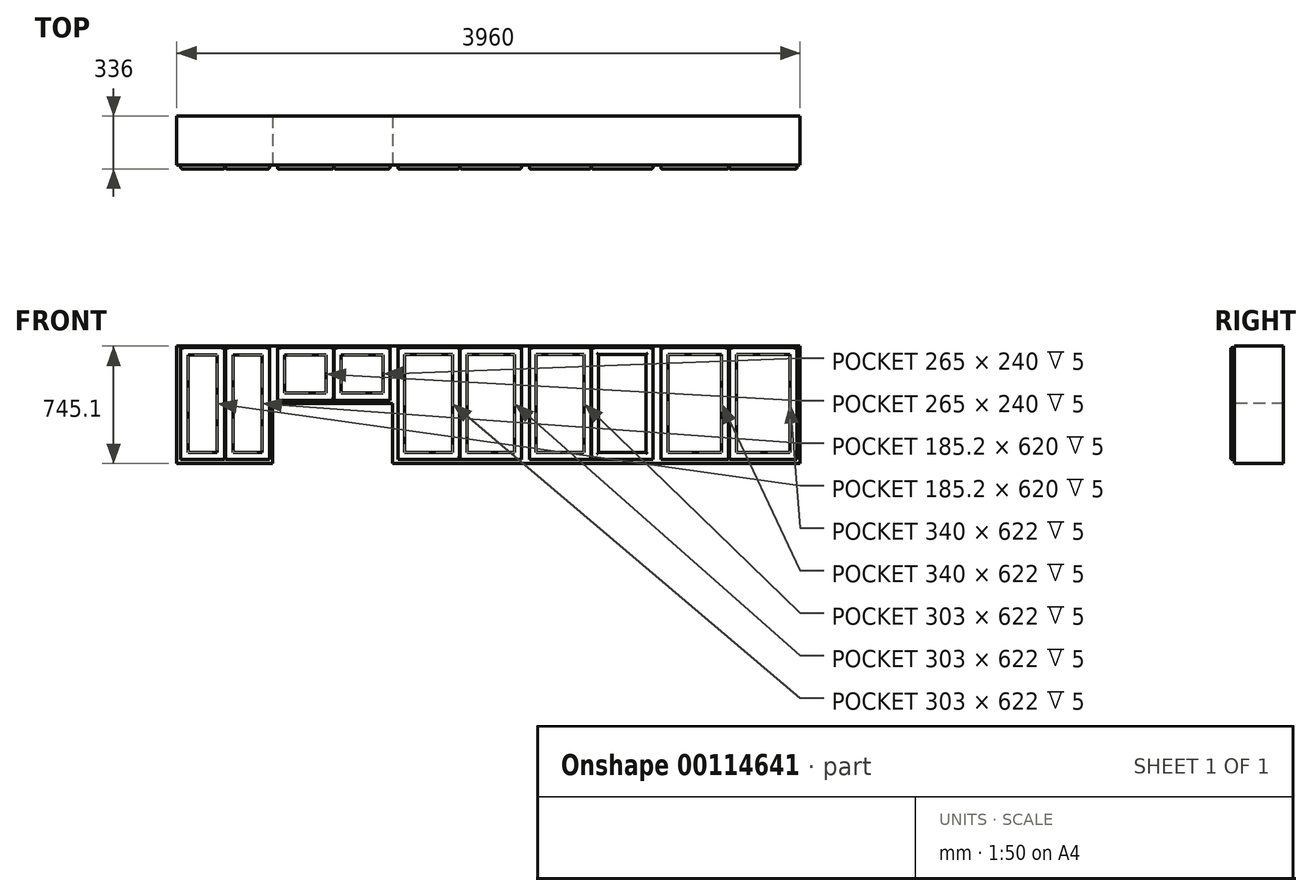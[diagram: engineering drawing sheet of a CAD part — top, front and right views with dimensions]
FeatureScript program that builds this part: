
annotation { "Feature Type Name" : "Feature", "Feature Type Description" : "" }
export const myFeature = defineFeature(function(context is Context, id is Id, definition is map)
    precondition{}
    {
        {
            var Q0;
            Q0=qCreatedBy(makeId("Front.planeOp"),FACE);
            var sketch = newSketch(context, id + "F0", { "sketchPlane" : qUnion([Q0])});
            skLineSegment(sketch, "E0.bottom", {"start": v(1980, -372.55) * mm, "end": v(-1980, -372.55) * mm});
            skLineSegment(sketch, "E0.top", {"start": v(1980, 372.55) * mm, "end": v(-1980, 372.55) * mm});
            skLineSegment(sketch, "E0.left", {"start": v(1980, -372.55) * mm, "end": v(1980, 372.55) * mm});
            skLineSegment(sketch, "E0.right", {"start": v(-1980, -372.55) * mm, "end": v(-1980, 372.55) * mm});
            skPoint(sketch, "E0.middle", {"position": v(0, 0) * mm});
            skSolve(sketch);
        }
        {
            var Q0;
            Q0=makeQuery(id+"F0.imprint","IMPRINT",FACE,{"disambiguationData":[TD([[makeQuery(id+"F0.imprint","IMPRINT",EDGE,{"derivedFrom":sQuery(id+"F0.wireOp",EDGE,"E0.bottom")}),-1.0]])]});
            extrude(context, id + "F1", {"entities" : qUnion([Q0]), "depth" : 311 * mm});
        }
        {
            var Q0;
            Q0=makeQuery(id+"F1.opExtrude","CAP_FACE",FACE,{"disambiguationData":[OSD([sQuery(id+"F0.wireOp",EDGE,"E0.bottom"),sQuery(id+"F0.wireOp",EDGE,"E0.top"),sQuery(id+"F0.wireOp",EDGE,"E0.left"),sQuery(id+"F0.wireOp",EDGE,"E0.right")])],"isStart":false});
            var sketch = newSketch(context, id + "F2", { "sketchPlane" : qUnion([Q0])});
            skLineSegment(sketch, "E1", {"start": v(-1370, -372.55) * mm, "end": v(-1370, 7.45) * mm});
            skLineSegment(sketch, "E2", {"start": v(-1370, 7.45) * mm, "end": v(-610, 7.45) * mm});
            skLineSegment(sketch, "E3", {"start": v(-610, 7.45) * mm, "end": v(-610, -372.55) * mm});
            skSolve(sketch);
        }
        {
            var Q0;
            {var subQ0=sQuery(id+"F2.wireOp",EDGE,"E1");Q0=makeQuery(id+"F2.imprint","IMPRINT",FACE,{"disambiguationData":[TD([[makeQuery(id+"F2.imprint","IMPRINT",EDGE,{"derivedFrom":subQ0}),-1.0]])]});}
            extrude(context, id + "F3", {"entities" : qUnion([Q0]), "operationType" : NewBodyOperationType.REMOVE, "endBound" : BoundingType.THROUGH_ALL, "oppositeDirection" : true, "depth" : 25 * mm});
        }
        {
            var Q0;
            Q0=makeQuery(id+"F1.opExtrude","CAP_FACE",FACE,{"disambiguationData":[OSD([sQuery(id+"F0.wireOp",EDGE,"E0.bottom"),sQuery(id+"F0.wireOp",EDGE,"E0.top"),sQuery(id+"F0.wireOp",EDGE,"E0.left"),sQuery(id+"F0.wireOp",EDGE,"E0.right")])],"isStart":false});
            var sketch = newSketch(context, id + "F4", { "sketchPlane" : qUnion([Q0])});
            skPoint(sketch, "E4.oppositeSnap0", {"position": v(-1675, -372.55) * mm});
            skLineSegment(sketch, "E4.bottom", {"start": v(-1955, 362.45) * mm, "end": v(-1675, 362.45) * mm});
            skLineSegment(sketch, "E4.top", {"start": v(-1955, -347.55) * mm, "end": v(-1675, -347.55) * mm});
            skLineSegment(sketch, "E4.left", {"start": v(-1955, 362.45) * mm, "end": v(-1955, -347.55) * mm});
            skLineSegment(sketch, "E4.right", {"start": v(-1675, 362.45) * mm, "end": v(-1675, -347.55) * mm});
            skLineSegment(sketch, "E5.bottom", {"start": v(-1670, 362.45) * mm, "end": v(-1390, 362.45) * mm});
            skLineSegment(sketch, "E5.top", {"start": v(-1670, -347.55) * mm, "end": v(-1390, -347.55) * mm});
            skLineSegment(sketch, "E5.left", {"start": v(-1670, 362.45) * mm, "end": v(-1670, -347.55) * mm});
            skLineSegment(sketch, "E5.right", {"start": v(-1390, 362.45) * mm, "end": v(-1390, -347.55) * mm});
            skLineSegment(sketch, "E6.bottom", {"start": v(-1340, 362.45) * mm, "end": v(-985, 362.45) * mm});
            skLineSegment(sketch, "E6.top", {"start": v(-1340, 27.45) * mm, "end": v(-985, 27.45) * mm});
            skLineSegment(sketch, "E6.left", {"start": v(-1340, 362.45) * mm, "end": v(-1340, 27.45) * mm});
            skLineSegment(sketch, "E6.right", {"start": v(-985, 362.45) * mm, "end": v(-985, 27.45) * mm});
            skLineSegment(sketch, "E7.bottom", {"start": v(-980, 362.45) * mm, "end": v(-625, 362.45) * mm});
            skLineSegment(sketch, "E7.top", {"start": v(-980, 27.45) * mm, "end": v(-625, 27.45) * mm});
            skLineSegment(sketch, "E7.left", {"start": v(-980, 362.45) * mm, "end": v(-980, 27.45) * mm});
            skLineSegment(sketch, "E7.right", {"start": v(-625, 362.45) * mm, "end": v(-625, 27.45) * mm});
            skLineSegment(sketch, "E8.bottom", {"start": v(-575, 362.45) * mm, "end": v(-185, 362.45) * mm});
            skLineSegment(sketch, "E8.top", {"start": v(-575, -347.55) * mm, "end": v(-185, -347.55) * mm});
            skLineSegment(sketch, "E8.left", {"start": v(-575, 362.45) * mm, "end": v(-575, -347.55) * mm});
            skLineSegment(sketch, "E8.right", {"start": v(-185, 362.45) * mm, "end": v(-185, -347.55) * mm});
            skLineSegment(sketch, "E9.bottom", {"start": v(-180, 362.45) * mm, "end": v(210, 362.45) * mm});
            skLineSegment(sketch, "E9.top", {"start": v(-180, -347.55) * mm, "end": v(210, -347.55) * mm});
            skLineSegment(sketch, "E9.left", {"start": v(-180, 362.45) * mm, "end": v(-180, -347.55) * mm});
            skLineSegment(sketch, "E9.right", {"start": v(210, 362.45) * mm, "end": v(210, -347.55) * mm});
            skLineSegment(sketch, "E10.bottom", {"start": v(260, 362.45) * mm, "end": v(650, 362.45) * mm});
            skLineSegment(sketch, "E10.top", {"start": v(260, -347.55) * mm, "end": v(650, -347.55) * mm});
            skLineSegment(sketch, "E10.left", {"start": v(260, 362.45) * mm, "end": v(260, -347.55) * mm});
            skLineSegment(sketch, "E10.right", {"start": v(650, 362.45) * mm, "end": v(650, -347.55) * mm});
            skLineSegment(sketch, "E11.bottom", {"start": v(655, 362.45) * mm, "end": v(1045, 362.45) * mm});
            skLineSegment(sketch, "E11.top", {"start": v(655, -347.55) * mm, "end": v(1045, -347.55) * mm});
            skLineSegment(sketch, "E11.left", {"start": v(655, 362.45) * mm, "end": v(655, -347.55) * mm});
            skLineSegment(sketch, "E11.right", {"start": v(1045, 362.45) * mm, "end": v(1045, -347.55) * mm});
            skLineSegment(sketch, "E12.bottom", {"start": v(1095, 362.45) * mm, "end": v(1525, 362.45) * mm});
            skLineSegment(sketch, "E12.top", {"start": v(1095, -347.55) * mm, "end": v(1525, -347.55) * mm});
            skLineSegment(sketch, "E12.left", {"start": v(1095, 362.45) * mm, "end": v(1095, -347.55) * mm});
            skLineSegment(sketch, "E12.right", {"start": v(1525, 362.45) * mm, "end": v(1525, -347.55) * mm});
            skLineSegment(sketch, "E13.bottom", {"start": v(1530, 362.45) * mm, "end": v(1960, 362.45) * mm});
            skLineSegment(sketch, "E13.top", {"start": v(1530, -347.55) * mm, "end": v(1960, -347.55) * mm});
            skLineSegment(sketch, "E13.left", {"start": v(1530, 362.45) * mm, "end": v(1530, -347.55) * mm});
            skLineSegment(sketch, "E13.right", {"start": v(1960, 362.45) * mm, "end": v(1960, -347.55) * mm});
            skSolve(sketch);
        }
        {
            var Q0;
            Q0 = qSketchRegion(id + "F4", true);
            extrude(context, id + "F5", {"entities" : qUnion([Q0]), "operationType" : NewBodyOperationType.ADD, "depth" : 25 * mm});
        }
        {
            var Q0;
            Q0=makeQuery(id+"F5.opExtrude","CAP_FACE",FACE,{"disambiguationData":[OSD([sQuery(id+"F4.wireOp",EDGE,"E4.bottom"),sQuery(id+"F4.wireOp",EDGE,"E4.top"),sQuery(id+"F4.wireOp",EDGE,"E4.left"),sQuery(id+"F4.wireOp",EDGE,"E4.right")])],"isStart":false});
            var sketch = newSketch(context, id + "F6", { "sketchPlane" : qUnion([Q0])});
            skLineSegment(sketch, "E14.bottom", {"start": v(-1907.7, 316.95) * mm, "end": v(-1722.5, 316.95) * mm});
            skLineSegment(sketch, "E14.top", {"start": v(-1907.7, -303.05) * mm, "end": v(-1722.5, -303.05) * mm});
            skLineSegment(sketch, "E14.left", {"start": v(-1907.7, 316.95) * mm, "end": v(-1907.7, -303.05) * mm});
            skLineSegment(sketch, "E14.right", {"start": v(-1722.5, 316.95) * mm, "end": v(-1722.5, -303.05) * mm});
            skLineSegment(sketch, "E15.bottom", {"start": v(-1622.5, 316.95) * mm, "end": v(-1437.3, 316.95) * mm});
            skLineSegment(sketch, "E15.top", {"start": v(-1622.5, -303.05) * mm, "end": v(-1437.3, -303.05) * mm});
            skLineSegment(sketch, "E15.left", {"start": v(-1622.5, 316.95) * mm, "end": v(-1622.5, -303.05) * mm});
            skLineSegment(sketch, "E15.right", {"start": v(-1437.3, 316.95) * mm, "end": v(-1437.3, -303.05) * mm});
            skLineSegment(sketch, "E16.bottom", {"start": v(-1295, 314.95) * mm, "end": v(-1030, 314.95) * mm});
            skLineSegment(sketch, "E16.top", {"start": v(-1295, 74.95) * mm, "end": v(-1030, 74.95) * mm});
            skLineSegment(sketch, "E16.left", {"start": v(-1295, 314.95) * mm, "end": v(-1295, 74.95) * mm});
            skLineSegment(sketch, "E16.right", {"start": v(-1030, 314.95) * mm, "end": v(-1030, 74.95) * mm});
            skLineSegment(sketch, "E17.bottom", {"start": v(-935, 314.95) * mm, "end": v(-670, 314.95) * mm});
            skLineSegment(sketch, "E17.top", {"start": v(-935, 74.95) * mm, "end": v(-670, 74.95) * mm});
            skLineSegment(sketch, "E17.left", {"start": v(-935, 314.95) * mm, "end": v(-935, 74.95) * mm});
            skLineSegment(sketch, "E17.right", {"start": v(-670, 314.95) * mm, "end": v(-670, 74.95) * mm});
            skSolve(sketch);
        }
        {
            var Q0;
            Q0=makeQuery(id+"F5.opExtrude","CAP_FACE",FACE,{"disambiguationData":[OSD([sQuery(id+"F4.wireOp",EDGE,"E10.bottom"),sQuery(id+"F4.wireOp",EDGE,"E10.top"),sQuery(id+"F4.wireOp",EDGE,"E10.left"),sQuery(id+"F4.wireOp",EDGE,"E10.right")])],"isStart":false});
            var sketch = newSketch(context, id + "F7", { "sketchPlane" : qUnion([Q0])});
            skLineSegment(sketch, "E18.bottom", {"start": v(-531.3, 318.45) * mm, "end": v(-228.3, 318.45) * mm});
            skLineSegment(sketch, "E18.top", {"start": v(-531.3, -303.55) * mm, "end": v(-228.3, -303.55) * mm});
            skLineSegment(sketch, "E18.left", {"start": v(-531.3, 318.45) * mm, "end": v(-531.3, -303.55) * mm});
            skLineSegment(sketch, "E18.right", {"start": v(-228.3, 318.45) * mm, "end": v(-228.3, -303.55) * mm});
            skLineSegment(sketch, "E19.bottom", {"start": v(-136.3, 318.45) * mm, "end": v(166.7, 318.45) * mm});
            skLineSegment(sketch, "E19.top", {"start": v(-136.3, -303.55) * mm, "end": v(166.7, -303.55) * mm});
            skLineSegment(sketch, "E19.left", {"start": v(-136.3, 318.45) * mm, "end": v(-136.3, -303.55) * mm});
            skLineSegment(sketch, "E19.right", {"start": v(166.7, 318.45) * mm, "end": v(166.7, -303.55) * mm});
            skLineSegment(sketch, "E20.bottom", {"start": v(303.7, 318.45) * mm, "end": v(606.7, 318.45) * mm});
            skLineSegment(sketch, "E20.top", {"start": v(303.7, -303.55) * mm, "end": v(606.7, -303.55) * mm});
            skLineSegment(sketch, "E20.left", {"start": v(303.7, 318.45) * mm, "end": v(303.7, -303.55) * mm});
            skLineSegment(sketch, "E20.right", {"start": v(606.7, 318.45) * mm, "end": v(606.7, -303.55) * mm});
            skLineSegment(sketch, "E21.bottom", {"start": v(698.7, 318.45) * mm, "end": v(1001.7, 318.45) * mm});
            skLineSegment(sketch, "E21.top", {"start": v(698.7, -303.55) * mm, "end": v(1001.7, -303.55) * mm});
            skLineSegment(sketch, "E21.left", {"start": v(698.7, 318.45) * mm, "end": v(698.7, -303.55) * mm});
            skLineSegment(sketch, "E21.right", {"start": v(1001.7, 318.45) * mm, "end": v(1001.7, -303.55) * mm});
            skLineSegment(sketch, "E22.bottom", {"start": v(1140, 318.45) * mm, "end": v(1480, 318.45) * mm});
            skLineSegment(sketch, "E22.top", {"start": v(1140, -303.55) * mm, "end": v(1480, -303.55) * mm});
            skLineSegment(sketch, "E22.left", {"start": v(1140, 318.45) * mm, "end": v(1140, -303.55) * mm});
            skLineSegment(sketch, "E22.right", {"start": v(1480, 318.45) * mm, "end": v(1480, -303.55) * mm});
            skLineSegment(sketch, "E23.bottom", {"start": v(1575, 318.45) * mm, "end": v(1915, 318.45) * mm});
            skLineSegment(sketch, "E23.top", {"start": v(1575, -303.55) * mm, "end": v(1915, -303.55) * mm});
            skLineSegment(sketch, "E23.left", {"start": v(1575, 318.45) * mm, "end": v(1575, -303.55) * mm});
            skLineSegment(sketch, "E23.right", {"start": v(1915, 318.45) * mm, "end": v(1915, -303.55) * mm});
            skSolve(sketch);
        }
        {
            var Q0;
            Q0 = qSketchRegion(id + "F6", true);
            extrude(context, id + "F8", {"entities" : qUnion([Q0]), "operationType" : NewBodyOperationType.REMOVE, "oppositeDirection" : true, "depth" : 5 * mm});
        }
        {
            var Q0;
            Q0 = qSketchRegion(id + "F7", true);
            extrude(context, id + "F9", {"entities" : qUnion([Q0]), "operationType" : NewBodyOperationType.REMOVE, "oppositeDirection" : true, "depth" : 5 * mm});
        }
        {
            var Q0;
            Q0=makeQuery(id+"F5.opExtrude","CAP_EDGE",EDGE,{"disambiguationData":[OSD([sQuery(id+"F4.wireOp",EDGE,"E4.bottom")])],"isStart":false});
            var Q1;
            Q1=makeQuery(id+"F5.opExtrude","CAP_EDGE",EDGE,{"disambiguationData":[OSD([sQuery(id+"F4.wireOp",EDGE,"E4.left")])],"isStart":false});
            var Q2;
            Q2=makeQuery(id+"F5.opExtrude","CAP_EDGE",EDGE,{"disambiguationData":[OSD([sQuery(id+"F4.wireOp",EDGE,"E4.right")])],"isStart":false});
            var Q3;
            Q3=makeQuery(id+"F5.opExtrude","CAP_EDGE",EDGE,{"disambiguationData":[OSD([sQuery(id+"F4.wireOp",EDGE,"E4.top")])],"isStart":false});
            var Q4;
            Q4=makeQuery(id+"F5.opExtrude","CAP_EDGE",EDGE,{"disambiguationData":[OSD([sQuery(id+"F4.wireOp",EDGE,"E5.bottom")])],"isStart":false});
            var Q5;
            Q5=makeQuery(id+"F5.opExtrude","CAP_EDGE",EDGE,{"disambiguationData":[OSD([sQuery(id+"F4.wireOp",EDGE,"E5.left")])],"isStart":false});
            var Q6;
            Q6=makeQuery(id+"F5.opExtrude","CAP_EDGE",EDGE,{"disambiguationData":[OSD([sQuery(id+"F4.wireOp",EDGE,"E5.right")])],"isStart":false});
            var Q7;
            Q7=makeQuery(id+"F5.opExtrude","CAP_EDGE",EDGE,{"disambiguationData":[OSD([sQuery(id+"F4.wireOp",EDGE,"E5.top")])],"isStart":false});
            var Q8;
            Q8=makeQuery(id+"F5.opExtrude","CAP_EDGE",EDGE,{"disambiguationData":[OSD([sQuery(id+"F4.wireOp",EDGE,"E6.left")])],"isStart":false});
            var Q9;
            Q9=makeQuery(id+"F5.opExtrude","CAP_EDGE",EDGE,{"disambiguationData":[OSD([sQuery(id+"F4.wireOp",EDGE,"E6.bottom")])],"isStart":false});
            var Q10;
            Q10=makeQuery(id+"F5.opExtrude","CAP_EDGE",EDGE,{"disambiguationData":[OSD([sQuery(id+"F4.wireOp",EDGE,"E6.top")])],"isStart":false});
            var Q11;
            Q11=makeQuery(id+"F5.opExtrude","CAP_EDGE",EDGE,{"disambiguationData":[OSD([sQuery(id+"F4.wireOp",EDGE,"E6.right")])],"isStart":false});
            var Q12;
            Q12=makeQuery(id+"F5.opExtrude","CAP_EDGE",EDGE,{"disambiguationData":[OSD([sQuery(id+"F4.wireOp",EDGE,"E7.left")])],"isStart":false});
            var Q13;
            Q13=makeQuery(id+"F5.opExtrude","CAP_EDGE",EDGE,{"disambiguationData":[OSD([sQuery(id+"F4.wireOp",EDGE,"E7.top")])],"isStart":false});
            var Q14;
            Q14=makeQuery(id+"F5.opExtrude","CAP_EDGE",EDGE,{"disambiguationData":[OSD([sQuery(id+"F4.wireOp",EDGE,"E7.right")])],"isStart":false});
            var Q15;
            Q15=makeQuery(id+"F5.opExtrude","CAP_EDGE",EDGE,{"disambiguationData":[OSD([sQuery(id+"F4.wireOp",EDGE,"E7.bottom")])],"isStart":false});
            var Q16;
            Q16=makeQuery(id+"F5.opExtrude","CAP_EDGE",EDGE,{"disambiguationData":[OSD([sQuery(id+"F4.wireOp",EDGE,"E8.bottom")])],"isStart":false});
            var Q17;
            Q17=makeQuery(id+"F5.opExtrude","CAP_EDGE",EDGE,{"disambiguationData":[OSD([sQuery(id+"F4.wireOp",EDGE,"E8.left")])],"isStart":false});
            var Q18;
            Q18=makeQuery(id+"F5.opExtrude","CAP_EDGE",EDGE,{"disambiguationData":[OSD([sQuery(id+"F4.wireOp",EDGE,"E8.right")])],"isStart":false});
            var Q19;
            Q19=makeQuery(id+"F5.opExtrude","CAP_EDGE",EDGE,{"disambiguationData":[OSD([sQuery(id+"F4.wireOp",EDGE,"E8.top")])],"isStart":false});
            var Q20;
            Q20=makeQuery(id+"F5.opExtrude","CAP_EDGE",EDGE,{"disambiguationData":[OSD([sQuery(id+"F4.wireOp",EDGE,"E9.top")])],"isStart":false});
            var Q21;
            Q21=makeQuery(id+"F5.opExtrude","CAP_EDGE",EDGE,{"disambiguationData":[OSD([sQuery(id+"F4.wireOp",EDGE,"E9.left")])],"isStart":false});
            var Q22;
            Q22=makeQuery(id+"F5.opExtrude","CAP_EDGE",EDGE,{"disambiguationData":[OSD([sQuery(id+"F4.wireOp",EDGE,"E9.right")])],"isStart":false});
            var Q23;
            Q23=makeQuery(id+"F5.opExtrude","CAP_EDGE",EDGE,{"disambiguationData":[OSD([sQuery(id+"F4.wireOp",EDGE,"E9.bottom")])],"isStart":false});
            var Q24;
            Q24=makeQuery(id+"F5.opExtrude","CAP_EDGE",EDGE,{"disambiguationData":[OSD([sQuery(id+"F4.wireOp",EDGE,"E10.left")])],"isStart":false});
            var Q25;
            Q25=makeQuery(id+"F5.opExtrude","CAP_EDGE",EDGE,{"disambiguationData":[OSD([sQuery(id+"F4.wireOp",EDGE,"E10.bottom")])],"isStart":false});
            var Q26;
            Q26=makeQuery(id+"F5.opExtrude","CAP_EDGE",EDGE,{"disambiguationData":[OSD([sQuery(id+"F4.wireOp",EDGE,"E10.right")])],"isStart":false});
            var Q27;
            Q27=makeQuery(id+"F5.opExtrude","CAP_EDGE",EDGE,{"disambiguationData":[OSD([sQuery(id+"F4.wireOp",EDGE,"E10.top")])],"isStart":false});
            var Q28;
            Q28=makeQuery(id+"F5.opExtrude","CAP_EDGE",EDGE,{"disambiguationData":[OSD([sQuery(id+"F4.wireOp",EDGE,"E11.top")])],"isStart":false});
            var Q29;
            Q29=makeQuery(id+"F5.opExtrude","CAP_EDGE",EDGE,{"disambiguationData":[OSD([sQuery(id+"F4.wireOp",EDGE,"E11.left")])],"isStart":false});
            var Q30;
            Q30=makeQuery(id+"F5.opExtrude","CAP_EDGE",EDGE,{"disambiguationData":[OSD([sQuery(id+"F4.wireOp",EDGE,"E11.bottom")])],"isStart":false});
            var Q31;
            Q31=makeQuery(id+"F5.opExtrude","CAP_EDGE",EDGE,{"disambiguationData":[OSD([sQuery(id+"F4.wireOp",EDGE,"E11.right")])],"isStart":false});
            var Q32;
            Q32=makeQuery(id+"F5.opExtrude","CAP_EDGE",EDGE,{"disambiguationData":[OSD([sQuery(id+"F4.wireOp",EDGE,"E12.left")])],"isStart":false});
            var Q33;
            Q33=makeQuery(id+"F5.opExtrude","CAP_EDGE",EDGE,{"disambiguationData":[OSD([sQuery(id+"F4.wireOp",EDGE,"E12.bottom")])],"isStart":false});
            var Q34;
            Q34=makeQuery(id+"F5.opExtrude","CAP_EDGE",EDGE,{"disambiguationData":[OSD([sQuery(id+"F4.wireOp",EDGE,"E12.right")])],"isStart":false});
            var Q35;
            Q35=makeQuery(id+"F5.opExtrude","CAP_EDGE",EDGE,{"disambiguationData":[OSD([sQuery(id+"F4.wireOp",EDGE,"E12.top")])],"isStart":false});
            var Q36;
            Q36=makeQuery(id+"F5.opExtrude","CAP_EDGE",EDGE,{"disambiguationData":[OSD([sQuery(id+"F4.wireOp",EDGE,"E13.left")])],"isStart":false});
            var Q37;
            Q37=makeQuery(id+"F5.opExtrude","CAP_EDGE",EDGE,{"disambiguationData":[OSD([sQuery(id+"F4.wireOp",EDGE,"E13.bottom")])],"isStart":false});
            var Q38;
            Q38=makeQuery(id+"F5.opExtrude","CAP_EDGE",EDGE,{"disambiguationData":[OSD([sQuery(id+"F4.wireOp",EDGE,"E13.right")])],"isStart":false});
            var Q39;
            Q39=makeQuery(id+"F5.opExtrude","CAP_EDGE",EDGE,{"disambiguationData":[OSD([sQuery(id+"F4.wireOp",EDGE,"E13.top")])],"isStart":false});
            fillet(context, id + "F10", {"entities" : qUnion([Q0, Q1, Q2, Q3, Q4, Q5, Q6, Q7, Q8, Q9, Q10, Q11, Q12, Q13, Q14, Q15, Q16, Q17, Q18, Q19, Q20, Q21, Q22, Q23, Q24, Q25, Q26, Q27, Q28, Q29, Q30, Q31, Q32, Q33, Q34, Q35, Q36, Q37, Q38, Q39]), "radius" : 10 * mm, "tangentPropagation" : true, "allowEdgeOverflow" : false});
        }
        {
            var Q0;
            Q0=makeQuery(id+"F8.boolean.opBoolean","COPY",EDGE,{"derivedFrom":makeQuery(id+"F8.opExtrude","CAP_EDGE",EDGE,{"disambiguationData":[OSD([sQuery(id+"F6.wireOp",EDGE,"E14.left")])],"isStart":true})});
            var Q1;
            Q1=makeQuery(id+"F8.boolean.opBoolean","COPY",EDGE,{"derivedFrom":makeQuery(id+"F8.opExtrude","CAP_EDGE",EDGE,{"disambiguationData":[OSD([sQuery(id+"F6.wireOp",EDGE,"E14.bottom")])],"isStart":true})});
            var Q2;
            Q2=makeQuery(id+"F8.boolean.opBoolean","COPY",EDGE,{"derivedFrom":makeQuery(id+"F8.opExtrude","CAP_EDGE",EDGE,{"disambiguationData":[OSD([sQuery(id+"F6.wireOp",EDGE,"E14.right")])],"isStart":true})});
            var Q3;
            Q3=makeQuery(id+"F8.boolean.opBoolean","COPY",EDGE,{"derivedFrom":makeQuery(id+"F8.opExtrude","CAP_EDGE",EDGE,{"disambiguationData":[OSD([sQuery(id+"F6.wireOp",EDGE,"E14.top")])],"isStart":true})});
            var Q4;
            Q4=makeQuery(id+"F8.boolean.opBoolean","COPY",EDGE,{"derivedFrom":makeQuery(id+"F8.opExtrude","CAP_EDGE",EDGE,{"disambiguationData":[OSD([sQuery(id+"F6.wireOp",EDGE,"E15.left")])],"isStart":true})});
            var Q5;
            Q5=makeQuery(id+"F8.boolean.opBoolean","COPY",EDGE,{"derivedFrom":makeQuery(id+"F8.opExtrude","CAP_EDGE",EDGE,{"disambiguationData":[OSD([sQuery(id+"F6.wireOp",EDGE,"E15.top")])],"isStart":true})});
            var Q6;
            Q6=makeQuery(id+"F8.boolean.opBoolean","COPY",EDGE,{"derivedFrom":makeQuery(id+"F8.opExtrude","CAP_EDGE",EDGE,{"disambiguationData":[OSD([sQuery(id+"F6.wireOp",EDGE,"E15.right")])],"isStart":true})});
            var Q7;
            Q7=makeQuery(id+"F8.boolean.opBoolean","COPY",EDGE,{"derivedFrom":makeQuery(id+"F8.opExtrude","CAP_EDGE",EDGE,{"disambiguationData":[OSD([sQuery(id+"F6.wireOp",EDGE,"E15.bottom")])],"isStart":true})});
            var Q8;
            Q8=makeQuery(id+"F8.boolean.opBoolean","COPY",EDGE,{"derivedFrom":makeQuery(id+"F8.opExtrude","CAP_EDGE",EDGE,{"disambiguationData":[OSD([sQuery(id+"F6.wireOp",EDGE,"E16.left")])],"isStart":true})});
            var Q9;
            Q9=makeQuery(id+"F8.boolean.opBoolean","COPY",EDGE,{"derivedFrom":makeQuery(id+"F8.opExtrude","CAP_EDGE",EDGE,{"disambiguationData":[OSD([sQuery(id+"F6.wireOp",EDGE,"E16.top")])],"isStart":true})});
            var Q10;
            Q10=makeQuery(id+"F8.boolean.opBoolean","COPY",EDGE,{"derivedFrom":makeQuery(id+"F8.opExtrude","CAP_EDGE",EDGE,{"disambiguationData":[OSD([sQuery(id+"F6.wireOp",EDGE,"E17.left")])],"isStart":true})});
            var Q11;
            Q11=makeQuery(id+"F8.boolean.opBoolean","COPY",EDGE,{"derivedFrom":makeQuery(id+"F8.opExtrude","CAP_EDGE",EDGE,{"disambiguationData":[OSD([sQuery(id+"F6.wireOp",EDGE,"E17.bottom")])],"isStart":true})});
            var Q12;
            Q12=makeQuery(id+"F8.boolean.opBoolean","COPY",EDGE,{"derivedFrom":makeQuery(id+"F8.opExtrude","CAP_EDGE",EDGE,{"disambiguationData":[OSD([sQuery(id+"F6.wireOp",EDGE,"E17.right")])],"isStart":true})});
            var Q13;
            Q13=makeQuery(id+"F8.boolean.opBoolean","COPY",EDGE,{"derivedFrom":makeQuery(id+"F8.opExtrude","CAP_EDGE",EDGE,{"disambiguationData":[OSD([sQuery(id+"F6.wireOp",EDGE,"E17.top")])],"isStart":true})});
            var Q14;
            Q14=makeQuery(id+"F9.boolean.opBoolean","COPY",EDGE,{"derivedFrom":makeQuery(id+"F9.opExtrude","CAP_EDGE",EDGE,{"disambiguationData":[OSD([sQuery(id+"F7.wireOp",EDGE,"E18.left")])],"isStart":true})});
            var Q15;
            Q15=makeQuery(id+"F9.boolean.opBoolean","COPY",EDGE,{"derivedFrom":makeQuery(id+"F9.opExtrude","CAP_EDGE",EDGE,{"disambiguationData":[OSD([sQuery(id+"F7.wireOp",EDGE,"E18.bottom")])],"isStart":true})});
            var Q16;
            Q16=makeQuery(id+"F9.boolean.opBoolean","COPY",EDGE,{"derivedFrom":makeQuery(id+"F9.opExtrude","CAP_EDGE",EDGE,{"disambiguationData":[OSD([sQuery(id+"F7.wireOp",EDGE,"E18.right")])],"isStart":true})});
            var Q17;
            Q17=makeQuery(id+"F9.boolean.opBoolean","COPY",EDGE,{"derivedFrom":makeQuery(id+"F9.opExtrude","CAP_EDGE",EDGE,{"disambiguationData":[OSD([sQuery(id+"F7.wireOp",EDGE,"E18.top")])],"isStart":true})});
            var Q18;
            Q18=makeQuery(id+"F9.boolean.opBoolean","COPY",EDGE,{"derivedFrom":makeQuery(id+"F9.opExtrude","CAP_EDGE",EDGE,{"disambiguationData":[OSD([sQuery(id+"F7.wireOp",EDGE,"E19.left")])],"isStart":true})});
            var Q19;
            Q19=makeQuery(id+"F9.boolean.opBoolean","COPY",EDGE,{"derivedFrom":makeQuery(id+"F9.opExtrude","CAP_EDGE",EDGE,{"disambiguationData":[OSD([sQuery(id+"F7.wireOp",EDGE,"E19.top")])],"isStart":true})});
            var Q20;
            Q20=makeQuery(id+"F9.boolean.opBoolean","COPY",EDGE,{"derivedFrom":makeQuery(id+"F9.opExtrude","CAP_EDGE",EDGE,{"disambiguationData":[OSD([sQuery(id+"F7.wireOp",EDGE,"E19.right")])],"isStart":true})});
            var Q21;
            Q21=makeQuery(id+"F9.boolean.opBoolean","COPY",EDGE,{"derivedFrom":makeQuery(id+"F9.opExtrude","CAP_EDGE",EDGE,{"disambiguationData":[OSD([sQuery(id+"F7.wireOp",EDGE,"E19.bottom")])],"isStart":true})});
            var Q22;
            Q22=makeQuery(id+"F9.boolean.opBoolean","COPY",EDGE,{"derivedFrom":makeQuery(id+"F9.opExtrude","CAP_EDGE",EDGE,{"disambiguationData":[OSD([sQuery(id+"F7.wireOp",EDGE,"E20.left")])],"isStart":true})});
            var Q23;
            Q23=makeQuery(id+"F9.boolean.opBoolean","COPY",EDGE,{"derivedFrom":makeQuery(id+"F9.opExtrude","CAP_EDGE",EDGE,{"disambiguationData":[OSD([sQuery(id+"F7.wireOp",EDGE,"E20.bottom")])],"isStart":true})});
            var Q24;
            Q24=makeQuery(id+"F9.boolean.opBoolean","COPY",EDGE,{"derivedFrom":makeQuery(id+"F9.opExtrude","CAP_EDGE",EDGE,{"disambiguationData":[OSD([sQuery(id+"F7.wireOp",EDGE,"E20.right")])],"isStart":true})});
            var Q25;
            Q25=makeQuery(id+"F9.boolean.opBoolean","COPY",EDGE,{"derivedFrom":makeQuery(id+"F9.opExtrude","CAP_EDGE",EDGE,{"disambiguationData":[OSD([sQuery(id+"F7.wireOp",EDGE,"E20.top")])],"isStart":true})});
            var Q26;
            Q26=makeQuery(id+"F9.boolean.opBoolean","COPY",EDGE,{"derivedFrom":makeQuery(id+"F9.opExtrude","CAP_EDGE",EDGE,{"disambiguationData":[OSD([sQuery(id+"F7.wireOp",EDGE,"E21.left")])],"isStart":true})});
            var Q27;
            Q27=makeQuery(id+"F9.boolean.opBoolean","COPY",EDGE,{"derivedFrom":makeQuery(id+"F9.opExtrude","CAP_EDGE",EDGE,{"disambiguationData":[OSD([sQuery(id+"F7.wireOp",EDGE,"E21.bottom")])],"isStart":true})});
            var Q28;
            Q28=makeQuery(id+"F9.boolean.opBoolean","COPY",EDGE,{"derivedFrom":makeQuery(id+"F9.opExtrude","CAP_EDGE",EDGE,{"disambiguationData":[OSD([sQuery(id+"F7.wireOp",EDGE,"E21.right")])],"isStart":true})});
            var Q29;
            Q29=makeQuery(id+"F5.opExtrude","CAP_FACE",FACE,{"disambiguationData":[OSD([sQuery(id+"F4.wireOp",EDGE,"E11.bottom"),sQuery(id+"F4.wireOp",EDGE,"E11.top"),sQuery(id+"F4.wireOp",EDGE,"E11.left"),sQuery(id+"F4.wireOp",EDGE,"E11.right")])],"isStart":false});
            var Q30;
            Q30=makeQuery(id+"F9.boolean.opBoolean","COPY",EDGE,{"derivedFrom":makeQuery(id+"F9.opExtrude","CAP_EDGE",EDGE,{"disambiguationData":[OSD([sQuery(id+"F7.wireOp",EDGE,"E21.top")])],"isStart":true})});
            var Q31;
            Q31=makeQuery(id+"F9.boolean.opBoolean","COPY",EDGE,{"derivedFrom":makeQuery(id+"F9.opExtrude","CAP_EDGE",EDGE,{"disambiguationData":[OSD([sQuery(id+"F7.wireOp",EDGE,"E22.bottom")])],"isStart":true})});
            var Q32;
            Q32=makeQuery(id+"F9.boolean.opBoolean","COPY",EDGE,{"derivedFrom":makeQuery(id+"F9.opExtrude","CAP_EDGE",EDGE,{"disambiguationData":[OSD([sQuery(id+"F7.wireOp",EDGE,"E22.left")])],"isStart":true})});
            var Q33;
            Q33=makeQuery(id+"F9.boolean.opBoolean","COPY",EDGE,{"derivedFrom":makeQuery(id+"F9.opExtrude","CAP_EDGE",EDGE,{"disambiguationData":[OSD([sQuery(id+"F7.wireOp",EDGE,"E22.right")])],"isStart":true})});
            var Q34;
            Q34=makeQuery(id+"F9.boolean.opBoolean","COPY",EDGE,{"derivedFrom":makeQuery(id+"F9.opExtrude","CAP_EDGE",EDGE,{"disambiguationData":[OSD([sQuery(id+"F7.wireOp",EDGE,"E22.top")])],"isStart":true})});
            var Q35;
            Q35=makeQuery(id+"F9.boolean.opBoolean","COPY",EDGE,{"derivedFrom":makeQuery(id+"F9.opExtrude","CAP_EDGE",EDGE,{"disambiguationData":[OSD([sQuery(id+"F7.wireOp",EDGE,"E23.top")])],"isStart":true})});
            var Q36;
            Q36=makeQuery(id+"F9.boolean.opBoolean","COPY",EDGE,{"derivedFrom":makeQuery(id+"F9.opExtrude","CAP_EDGE",EDGE,{"disambiguationData":[OSD([sQuery(id+"F7.wireOp",EDGE,"E23.left")])],"isStart":true})});
            var Q37;
            Q37=makeQuery(id+"F9.boolean.opBoolean","COPY",EDGE,{"derivedFrom":makeQuery(id+"F9.opExtrude","CAP_EDGE",EDGE,{"disambiguationData":[OSD([sQuery(id+"F7.wireOp",EDGE,"E23.bottom")])],"isStart":true})});
            var Q38;
            Q38=makeQuery(id+"F9.boolean.opBoolean","COPY",EDGE,{"derivedFrom":makeQuery(id+"F9.opExtrude","CAP_EDGE",EDGE,{"disambiguationData":[OSD([sQuery(id+"F7.wireOp",EDGE,"E23.right")])],"isStart":true})});
            var Q39;
            Q39=makeQuery(id+"F8.boolean.opBoolean","COPY",EDGE,{"derivedFrom":makeQuery(id+"F8.opExtrude","CAP_EDGE",EDGE,{"disambiguationData":[OSD([sQuery(id+"F6.wireOp",EDGE,"E16.bottom")])],"isStart":true})});
            var Q40;
            Q40=makeQuery(id+"F8.boolean.opBoolean","COPY",EDGE,{"derivedFrom":makeQuery(id+"F8.opExtrude","CAP_EDGE",EDGE,{"disambiguationData":[OSD([sQuery(id+"F6.wireOp",EDGE,"E16.right")])],"isStart":true})});
            fillet(context, id + "F11", {"entities" : qUnion([Q0, Q1, Q2, Q3, Q4, Q5, Q6, Q7, Q8, Q9, Q10, Q11, Q12, Q13, Q14, Q15, Q16, Q17, Q18, Q19, Q20, Q21, Q22, Q23, Q24, Q25, Q26, Q27, Q28, Q29, Q30, Q31, Q32, Q33, Q34, Q35, Q36, Q37, Q38, Q39, Q40]), "radius" : 10 * mm, "tangentPropagation" : true, "allowEdgeOverflow" : false});
        }
    });
